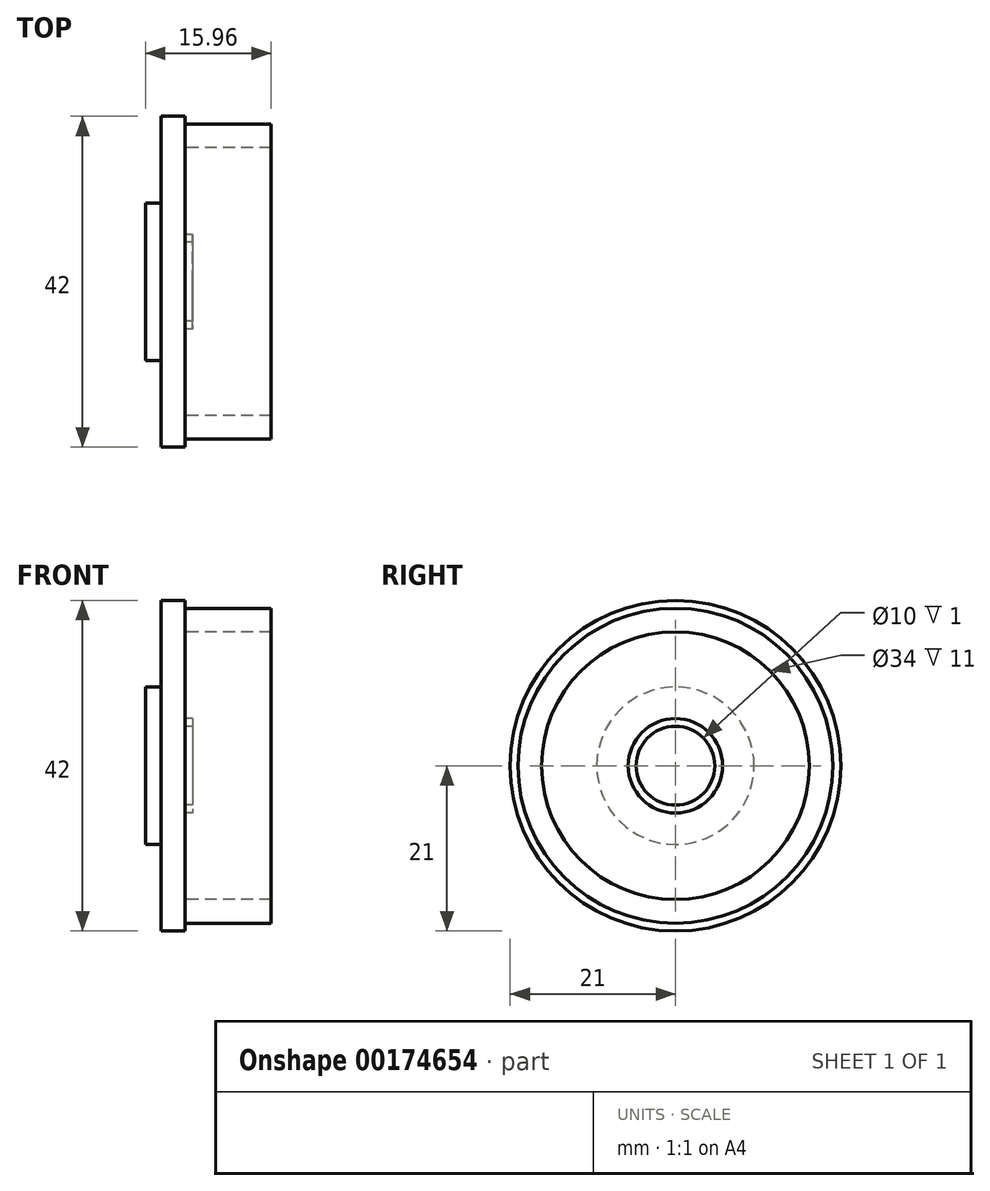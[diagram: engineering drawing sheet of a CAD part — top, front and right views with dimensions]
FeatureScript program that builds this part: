
annotation { "Feature Type Name" : "Feature", "Feature Type Description" : "" }
export const myFeature = defineFeature(function(context is Context, id is Id, definition is map)
    precondition{}
    {
        {
            var Q0;
            Q0=qCreatedBy(makeId("Front.planeOp"),FACE);
            var sketch = newSketch(context, id + "F0", { "sketchPlane" : qUnion([Q0])});
            skLineSegment(sketch, "E0.bottom", {"start": v(0, 0) * mm, "end": v(3, 0) * mm});
            skLineSegment(sketch, "E0.top", {"start": v(0, 21) * mm, "end": v(3, 21) * mm});
            skLineSegment(sketch, "E0.left", {"start": v(0, 0) * mm, "end": v(0, 21) * mm});
            skLineSegment(sketch, "E0.right", {"start": v(3, 0) * mm, "end": v(3, 21) * mm});
            skLineSegment(sketch, "E1.bottom", {"start": v(3, 0) * mm, "end": v(4, 0) * mm});
            skLineSegment(sketch, "E1.top", {"start": v(3, 6) * mm, "end": v(4, 6) * mm});
            skLineSegment(sketch, "E1.left", {"start": v(3, 0) * mm, "end": v(3, 6) * mm});
            skLineSegment(sketch, "E1.right", {"start": v(4, 0) * mm, "end": v(4, 6) * mm});
            skLineSegment(sketch, "E2.top", {"start": v(3, 5) * mm, "end": v(4, 5) * mm});
            skLineSegment(sketch, "E2.left", {"start": v(3, 0) * mm, "end": v(3, 5) * mm});
            skLineSegment(sketch, "E2.right", {"start": v(4, 0) * mm, "end": v(4, 5) * mm});
            skSolve(sketch);
        }
        {
            var Q0;
            Q0=qCreatedBy(makeId("Front.planeOp"),FACE);
            var sketch = newSketch(context, id + "F1", { "sketchPlane" : qUnion([Q0])});
            skLineSegment(sketch, "E3.bottom", {"start": v(0, 0) * mm, "end": v(-2, 0) * mm});
            skLineSegment(sketch, "E3.top", {"start": v(0, 10) * mm, "end": v(-2, 10) * mm});
            skLineSegment(sketch, "E3.left", {"start": v(0, 0) * mm, "end": v(0, 10) * mm});
            skLineSegment(sketch, "E3.right", {"start": v(-2, 0) * mm, "end": v(-2, 10) * mm});
            skLineSegment(sketch, "E4.bottom", {"start": v(2.96, 0) * mm, "end": v(13.96, 0) * mm});
            skLineSegment(sketch, "E4.top", {"start": v(2.96, 20) * mm, "end": v(13.96, 20) * mm});
            skLineSegment(sketch, "E4.left", {"start": v(2.96, 0) * mm, "end": v(2.96, 20) * mm});
            skLineSegment(sketch, "E4.right", {"start": v(13.96, 0) * mm, "end": v(13.96, 20) * mm});
            skLineSegment(sketch, "E5.top", {"start": v(2.96, 17) * mm, "end": v(13.96, 17) * mm});
            skLineSegment(sketch, "E5.left", {"start": v(2.96, 0) * mm, "end": v(2.96, 17) * mm});
            skLineSegment(sketch, "E5.right", {"start": v(13.96, 0) * mm, "end": v(13.96, 17) * mm});
            skSolve(sketch);
        }
        {
            var Q0;
            Q0=makeQuery(id+"F0.imprint","IMPRINT",FACE,{"disambiguationData":[TD([[makeQuery(id+"F0.imprint","IMPRINT",EDGE,{"derivedFrom":sQuery(id+"F0.wireOp",EDGE,"E1.top")}),-1.0]])]});
            var Q1;
            Q1=makeQuery(id+"F0.imprint","IMPRINT",FACE,{"disambiguationData":[TD([[makeQuery(id+"F0.imprint","IMPRINT",EDGE,{"derivedFrom":sQuery(id+"F0.wireOp",EDGE,"E0.bottom")}),1.0]])]});
            var Q2;
            Q2=makeQuery(id+"F1.imprint","IMPRINT",FACE,{"disambiguationData":[TD([[makeQuery(id+"F1.imprint","IMPRINT",EDGE,{"derivedFrom":sQuery(id+"F1.wireOp",EDGE,"E4.top")}),-1.0]])]});
            var Q3;
            Q3=makeQuery(id+"F1.imprint","IMPRINT",FACE,{"disambiguationData":[TD([[makeQuery(id+"F1.imprint","IMPRINT",EDGE,{"derivedFrom":sQuery(id+"F1.wireOp",EDGE,"E3.bottom")}),-1.0]])]});
            var Q4;
            Q4=sQuery(id+"F1.wireOp",EDGE,"E4.bottom");
            revolve(context, id + "F2", {"entities" : qUnion([Q0, Q1, Q2, Q3]), "axis" : qUnion([Q4]), "revolveType" : RevolveType.FULL});
        }
    });
